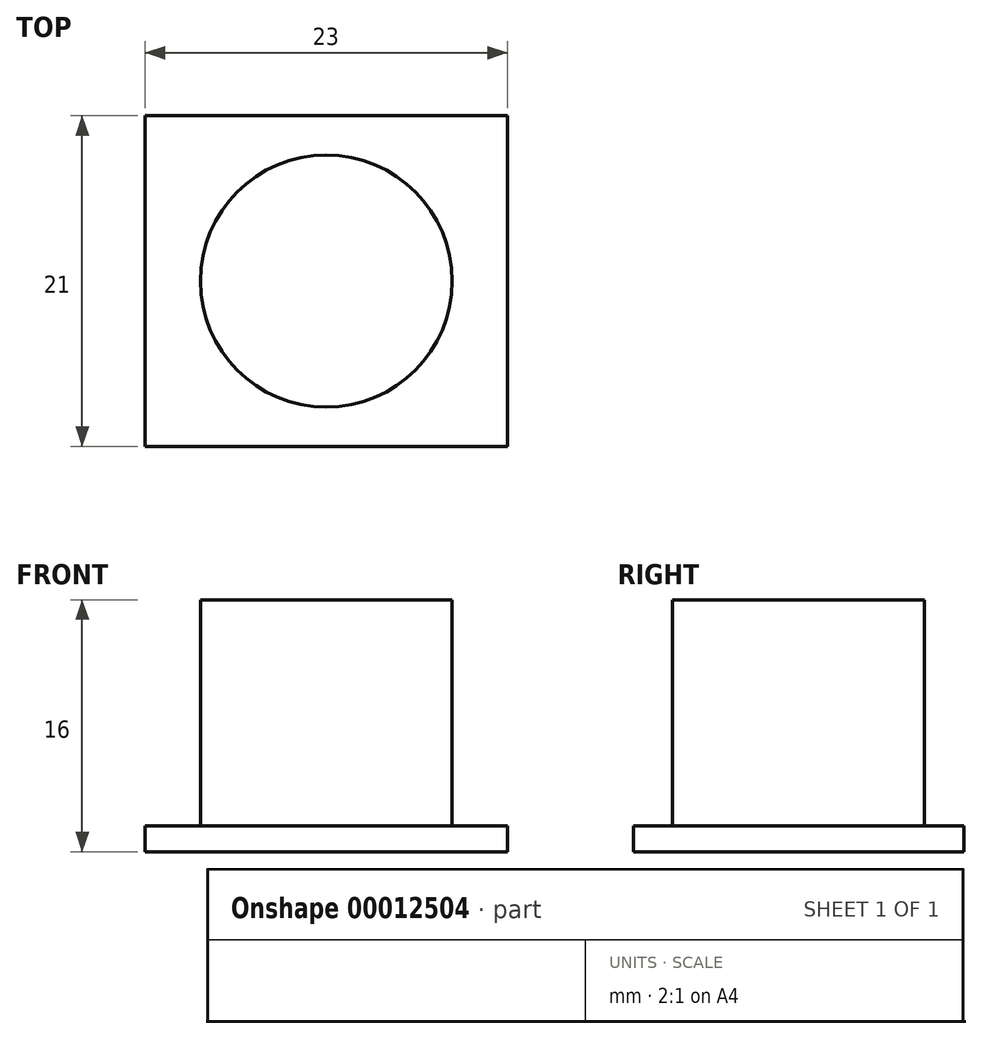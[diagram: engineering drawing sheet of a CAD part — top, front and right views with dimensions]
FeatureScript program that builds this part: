
annotation { "Feature Type Name" : "Feature", "Feature Type Description" : "" }
export const myFeature = defineFeature(function(context is Context, id is Id, definition is map)
    precondition{}
    {
        {
            var Q0;
            Q0=qCreatedBy(makeId("Top.planeOp"),FACE);
            var sketch = newSketch(context, id + "F0", { "sketchPlane" : qUnion([Q0])});
            skLineSegment(sketch, "E0.rect.bottom", {"start": v(11.5, -10.5) * mm, "end": v(-11.5, -10.5) * mm});
            skLineSegment(sketch, "E0.rect.top", {"start": v(11.5, 10.5) * mm, "end": v(-11.5, 10.5) * mm});
            skLineSegment(sketch, "E0.rect.left", {"start": v(11.5, -10.5) * mm, "end": v(11.5, 10.5) * mm});
            skLineSegment(sketch, "E0.rect.right", {"start": v(-11.5, -10.5) * mm, "end": v(-11.5, 10.5) * mm});
            skPoint(sketch, "E0.rect.middle", {"position": v(0, 0) * mm});
            skSolve(sketch);
        }
        {
            var Q0;
            Q0=qCreatedBy(makeId("Top.planeOp"),FACE);
            var sketch = newSketch(context, id + "F1", { "sketchPlane" : qUnion([Q0])});
            skCircle(sketch, "E1", {"center": v(0, 0) * mm, "radius": 8 * mm});
            skSolve(sketch);
        }
        {
            var Q0;
            Q0=makeQuery(id+"F0.imprint","IMPRINT",FACE,{"disambiguationData":[TD([[makeQuery(id+"F0.imprint","IMPRINT",EDGE,{"derivedFrom":sQuery(id+"F0.wireOp",EDGE,"E0.rect.bottom")}),-1.0]])]});
            extrude(context, id + "F2", {"entities" : qUnion([Q0]), "depth" : 1.63 * mm});
        }
        {
            var Q0;
            Q0=makeQuery(id+"F1.imprint","IMPRINT",FACE,{"disambiguationData":[TD([[makeQuery(id+"F1.imprint","IMPRINT",EDGE,{"derivedFrom":sQuery(id+"F1.wireOp",EDGE,"E1")}),1.0]])]});
            extrude(context, id + "F3", {"entities" : qUnion([Q0]), "operationType" : NewBodyOperationType.ADD, "depth" : 16 * mm});
        }
    });
